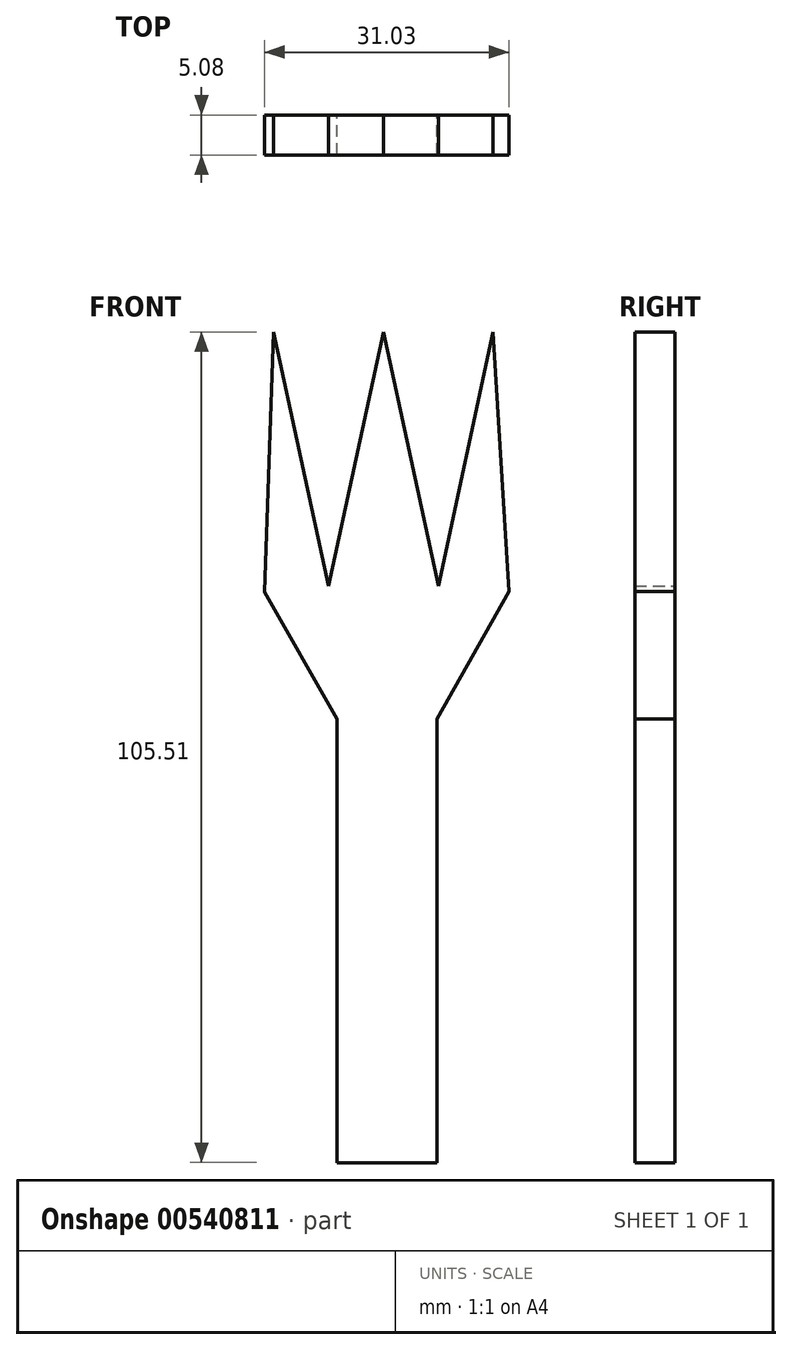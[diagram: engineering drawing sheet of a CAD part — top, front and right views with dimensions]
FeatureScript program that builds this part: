
annotation { "Feature Type Name" : "Feature", "Feature Type Description" : "" }
export const myFeature = defineFeature(function(context is Context, id is Id, definition is map)
    precondition{}
    {
        {
            var Q0;
            Q0=qCreatedBy(makeId("Front.planeOp"),FACE);
            var sketch = newSketch(context, id + "F0", { "sketchPlane" : qUnion([Q0])});
            skLineSegment(sketch, "E0", {"start": v(-40.83, 10.15) * mm, "end": v(-39.7, 43.15) * mm});
            skLineSegment(sketch, "E1", {"start": v(-39.7, 43.15) * mm, "end": v(-32.72, 10.88) * mm});
            skLineSegment(sketch, "E2", {"start": v(-32.72, 10.88) * mm, "end": v(-25.75, 43.15) * mm});
            skLineSegment(sketch, "E3", {"start": v(-25.75, 43.15) * mm, "end": v(-18.77, 10.88) * mm});
            skLineSegment(sketch, "E4", {"start": v(-18.77, 10.88) * mm, "end": v(-11.8, 43.15) * mm});
            skLineSegment(sketch, "E5", {"start": v(-11.8, 43.15) * mm, "end": v(-9.8, 10.2) * mm});
            skLineSegment(sketch, "E6", {"start": v(-9.8, 10.2) * mm, "end": v(-18.93, -5.99) * mm});
            skLineSegment(sketch, "E7", {"start": v(-18.93, -5.99) * mm, "end": v(-18.93, -62.36) * mm});
            skLineSegment(sketch, "E8", {"start": v(-18.93, -62.36) * mm, "end": v(-31.63, -62.36) * mm});
            skLineSegment(sketch, "E9", {"start": v(-31.63, -62.36) * mm, "end": v(-31.63, -5.99) * mm});
            skLineSegment(sketch, "E10", {"start": v(-31.63, -5.99) * mm, "end": v(-40.83, 10.15) * mm});
            skSolve(sketch);
        }
        {
            var Q0;
            Q0 = qSketchRegion(id + "F0", true);
            extrude(context, id + "F1", {"entities" : qUnion([Q0]), "depth" : 5.08 * mm, "offsetDistance" : 25.4 * mm});
        }
    });
